# Revit family: Thorn CETUS3 S
name_source: partatom
category: Lighting Fixtures
revit_build: Autodesk Revit 2016 (Build: 20150220_1215(x64)
units: mm (PartAtom-declared; Revit-internal decimal feet)

## family parameters
Cut with Voids When Loaded = No
Host = Face
Light Source = Yes
OmniClass Number = 23.80.70.11
OmniClass Title = Luminaries for Internal Lighting
Part Type = Normal
Room Calculation Point = No
Round Connector Dimension = Use Diameter
Shared = No

## types (2) — shared parameters
Apparent Load = 7 VA
Assembly Code = D5020200
Body = Thorn_Metal_White
Color Filter = 16777215
Description = Recessed LED luminaire
Dimming Lamp Color Temperature Shift = <None>
Emit Shape Visible in Rendering = No
Emit from Circle Diameter = 86 mm  [stored 0.282152 ft]
Height = 80 mm
Lamp = LED
Length = 137 mm
Manufacturer = Thorn Lighting
Tilt Angle = -90.00°
Voltage = 230 V
Width = 137 mm
zero-valued in all types: Default Elevation

## per-type parameters (varying)
| type | Model | Photometric Web File | URL |
| CETUS3 S 800-840 HF RWH | 96634886 | 96634886_(STD).IES | www.thornlighting.com/96634886 |
| CETUS3 S 800-840 HF E3D RWH | 92943893 | 92943893_(STD).IES | www.thornlighting.com/92943893 |

note: [stored X ft] marks values corroborated as IEEE doubles in the binary element streams (Revit-internal decimal feet)

## geometry (parser evidence)
native form markers: Sweep x2
no freeform markers — native parametric forms only
